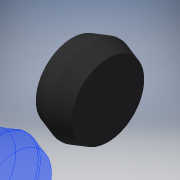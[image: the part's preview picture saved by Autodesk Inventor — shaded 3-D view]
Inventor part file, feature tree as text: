
AUTODESK INVENTOR PART (.ipt)
format: ipt  version: 2019 (Build 230136000, 136)  size: 111,104 bytes
history: native  units: mm
features: extrude x2, chamfer x2, sketch x2, other x1
ambient origin geometry x8: Origin, YZ Plane, XZ Plane, XY Plane, X Axis, Y Axis, Z Axis, Center Point
bodies: Body1 (feature_tree)
feature tree (7):
  other  "솔리드1"
  extrude  "돌출1"  Depth=75.0mm
  chamfer  "모따기1"  Distance=32.0mm
  chamfer  "모따기2"  Distance=5.0mm Angle=45.0deg
  extrude  "돌출2"  Depth=5.0mm TaperAngle=45.0deg
  sketch  "스케치1"
  sketch  "스케치2"
